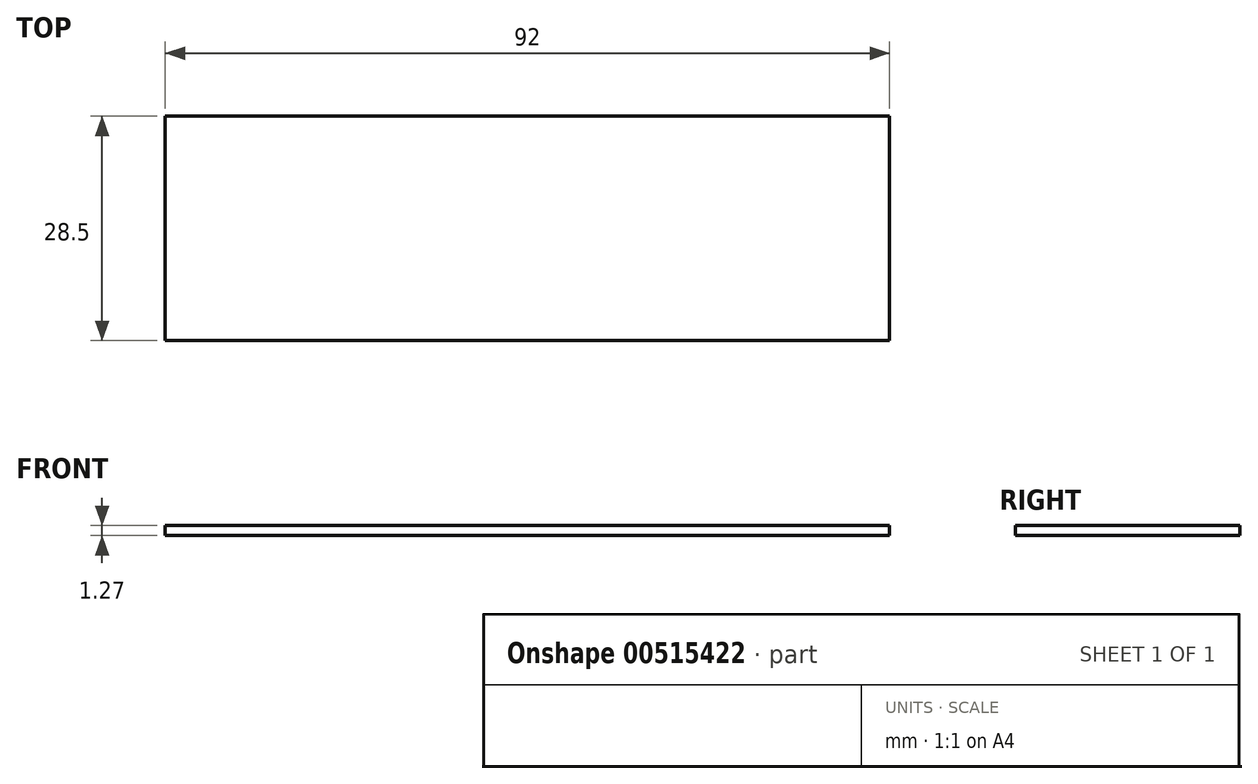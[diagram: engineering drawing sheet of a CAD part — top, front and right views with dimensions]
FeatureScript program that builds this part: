
annotation { "Feature Type Name" : "Feature", "Feature Type Description" : "" }
export const myFeature = defineFeature(function(context is Context, id is Id, definition is map)
    precondition{}
    {
        {
            var Q0;
            Q0=qCreatedBy(makeId("Top.planeOp"),FACE);
            var sketch = newSketch(context, id + "F0", { "sketchPlane" : qUnion([Q0])});
            skLineSegment(sketch, "E0.bottom", {"start": v(-46, -14.25) * mm, "end": v(46, -14.25) * mm});
            skLineSegment(sketch, "E0.top", {"start": v(-46, 14.25) * mm, "end": v(46, 14.25) * mm});
            skLineSegment(sketch, "E0.left", {"start": v(-46, -14.25) * mm, "end": v(-46, 14.25) * mm});
            skLineSegment(sketch, "E0.right", {"start": v(46, -14.25) * mm, "end": v(46, 14.25) * mm});
            skSolve(sketch);
        }
        {
            var Q0;
            Q0=makeQuery(id+"F0.imprint","IMPRINT",FACE,{"disambiguationData":[TD([[makeQuery(id+"F0.imprint","IMPRINT",EDGE,{"derivedFrom":sQuery(id+"F0.wireOp",EDGE,"E0.bottom")}),1.0]])]});
            extrude(context, id + "F1", {"entities" : qUnion([Q0]), "depth" : 1.27 * mm, "offsetDistance" : 25.4 * mm});
        }
    });
